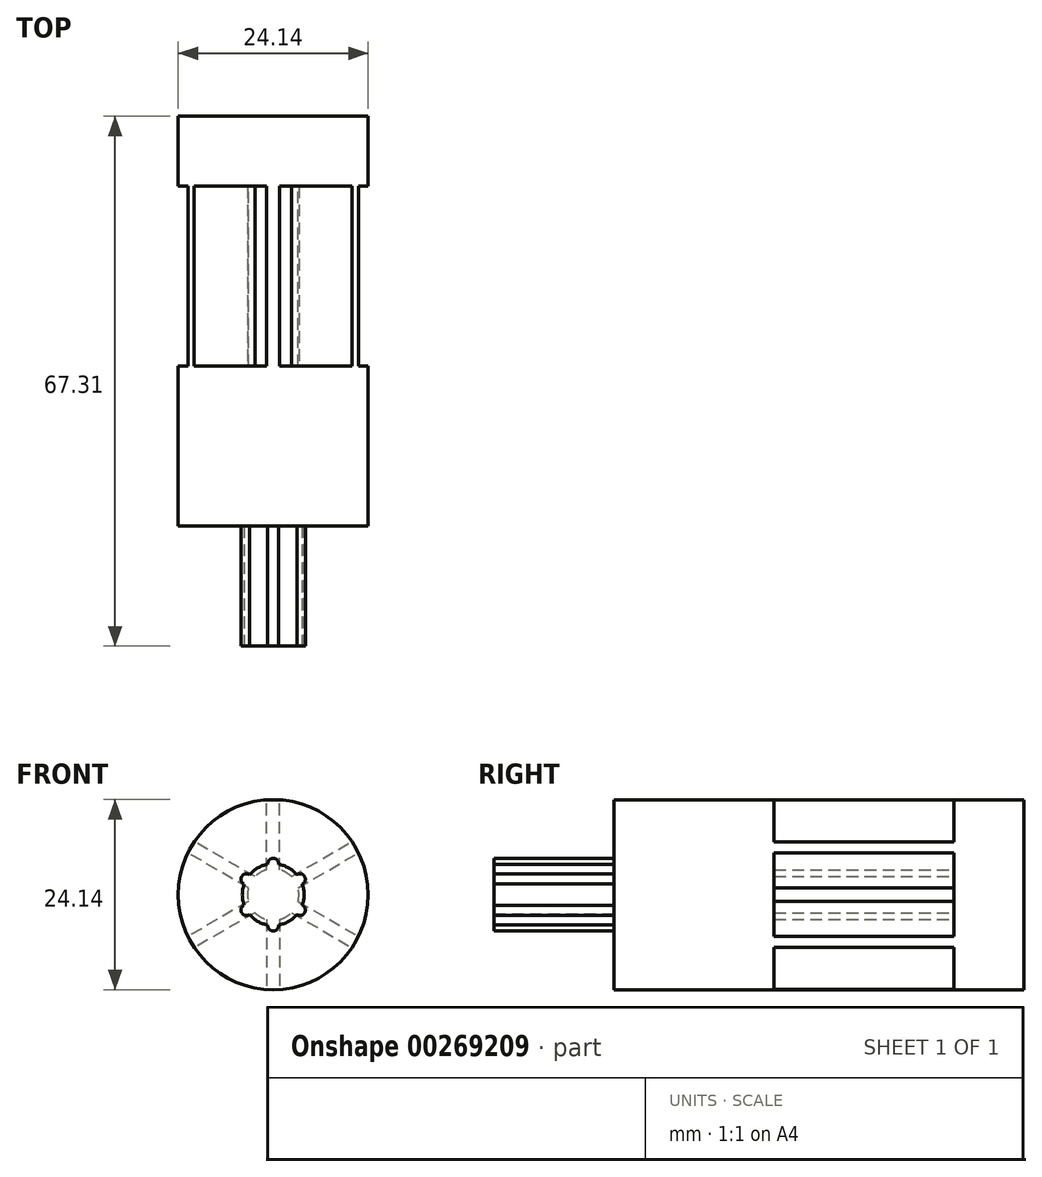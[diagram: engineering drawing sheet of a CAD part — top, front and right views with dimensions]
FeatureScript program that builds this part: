
annotation { "Feature Type Name" : "Feature", "Feature Type Description" : "" }
export const myFeature = defineFeature(function(context is Context, id is Id, definition is map)
    precondition{}
    {
        {
            var Q0;
            Q0=qCreatedBy(makeId("Front.planeOp"),FACE);
            var sketch = newSketch(context, id + "F0", { "sketchPlane" : qUnion([Q0])});
            skCircle(sketch, "E0", {"center": v(0, 0) * mm, "radius": 12.07 * mm});
            skCircle(sketch, "E1", {"center": v(0, 0) * mm, "radius": 3.27 * mm});
            skLineSegment(sketch, "E2", {"start": v(-0.82, 12.04) * mm, "end": v(-0.82, 3.16) * mm});
            skLineSegment(sketch, "E3.MirrorCS", {"start": v(0.82, 12.04) * mm, "end": v(0.82, 3.16) * mm});
            skLineSegment(sketch, "E4.1.0", {"start": v(-10.83, 5.31) * mm, "end": v(-3.15, 0.87) * mm});
            skLineSegment(sketch, "E4.1.1", {"start": v(-10.02, 6.73) * mm, "end": v(-2.33, 2.29) * mm});
            skLineSegment(sketch, "E4.2.0", {"start": v(-10.02, -6.73) * mm, "end": v(-2.33, -2.29) * mm});
            skLineSegment(sketch, "E4.2.1", {"start": v(-10.83, -5.31) * mm, "end": v(-3.15, -0.87) * mm});
            skLineSegment(sketch, "E4.3.0", {"start": v(0.82, -12.04) * mm, "end": v(0.82, -3.16) * mm});
            skLineSegment(sketch, "E4.3.1", {"start": v(-0.82, -12.04) * mm, "end": v(-0.82, -3.16) * mm});
            skLineSegment(sketch, "E4.4.0", {"start": v(10.83, -5.31) * mm, "end": v(3.15, -0.87) * mm});
            skLineSegment(sketch, "E4.4.1", {"start": v(10.02, -6.73) * mm, "end": v(2.33, -2.29) * mm});
            skLineSegment(sketch, "E4.5.0", {"start": v(10.02, 6.73) * mm, "end": v(2.33, 2.29) * mm});
            skLineSegment(sketch, "E4.5.1", {"start": v(10.83, 5.31) * mm, "end": v(3.15, 0.87) * mm});
            skSolve(sketch);
        }
        {
            var Q0;
            Q0=makeQuery(id+"F0.imprint","IMPRINT",FACE,{"disambiguationData":[TD([[makeQuery(id+"F0.imprint","IMPRINT",EDGE,{"derivedFrom":sQuery(id+"F0.wireOp",EDGE,"E1")}),1.0]])]});
            var Q1;
            Q1=makeQuery(id+"F0.imprint","IMPRINT",FACE,{"disambiguationData":[TD([[makeQuery(id+"F0.imprint","IMPRINT",EDGE,{"derivedFrom":sQuery(id+"F0.wireOp",EDGE,"E0")}),1.0]])]});
            extrude(context, id + "F1", {"entities" : qUnion([Q0, Q1]), "endBound" : BoundingType.SYMMETRIC, "depth" : 27.94 * mm});
        }
        {
            var Q0;
            Q0=makeQuery(id+"F0.imprint","IMPRINT",FACE,{"disambiguationData":[TD([[makeQuery(id+"F0.imprint","IMPRINT",EDGE,{"derivedFrom":sQuery(id+"F0.wireOp",EDGE,"E0")}),1.0]])]});
            extrude(context, id + "F2", {"entities" : qUnion([Q0]), "operationType" : NewBodyOperationType.REMOVE, "endBound" : BoundingType.SYMMETRIC, "oppositeDirection" : true, "depth" : 22.86 * mm});
        }
        {
            var Q0;
            {var subQ0=sQuery(id+"F0.wireOp",EDGE,"E2");Q0=makeQuery(id+"F0.imprint","IMPRINT",FACE,{"disambiguationData":[TD([[makeQuery(id+"F0.imprint","IMPRINT",EDGE,{"derivedFrom":subQ0}),1.0]])]});}
            var Q1;
            {var subQ0=sQuery(id+"F0.wireOp",EDGE,"E4.1.0");Q1=makeQuery(id+"F0.imprint","IMPRINT",FACE,{"disambiguationData":[TD([[makeQuery(id+"F0.imprint","IMPRINT",EDGE,{"derivedFrom":subQ0}),1.0]])]});}
            var Q2;
            {var subQ0=sQuery(id+"F0.wireOp",EDGE,"E4.2.0");Q2=makeQuery(id+"F0.imprint","IMPRINT",FACE,{"disambiguationData":[TD([[makeQuery(id+"F0.imprint","IMPRINT",EDGE,{"derivedFrom":subQ0}),1.0]])]});}
            var Q3;
            {var subQ0=sQuery(id+"F0.wireOp",EDGE,"E4.3.0");Q3=makeQuery(id+"F0.imprint","IMPRINT",FACE,{"disambiguationData":[TD([[makeQuery(id+"F0.imprint","IMPRINT",EDGE,{"derivedFrom":subQ0}),1.0]])]});}
            var Q4;
            {var subQ0=sQuery(id+"F0.wireOp",EDGE,"E4.5.0");Q4=makeQuery(id+"F0.imprint","IMPRINT",FACE,{"disambiguationData":[TD([[makeQuery(id+"F0.imprint","IMPRINT",EDGE,{"derivedFrom":subQ0}),1.0]])]});}
            var Q5;
            {var subQ0=sQuery(id+"F0.wireOp",EDGE,"E4.4.0");Q5=makeQuery(id+"F0.imprint","IMPRINT",FACE,{"disambiguationData":[TD([[makeQuery(id+"F0.imprint","IMPRINT",EDGE,{"derivedFrom":subQ0}),1.0]])]});}
            extrude(context, id + "F3", {"entities" : qUnion([Q0, Q1, Q2, Q3, Q4, Q5]), "operationType" : NewBodyOperationType.ADD, "endBound" : BoundingType.SYMMETRIC, "depth" : 25.4 * mm});
        }
        {
            var Q0;
            Q0=makeQuery(id+"F1.opExtrude","CAP_FACE",FACE,{"disambiguationData":[OSD([sQuery(id+"F0.wireOp",EDGE,"E0")])],"isStart":false});
            var sketch = newSketch(context, id + "F4", { "sketchPlane" : qUnion([Q0])});
            skCircle(sketch, "E5", {"center": v(0, 0) * mm, "radius": 3.92 * mm});
            skSolve(sketch);
        }
        {
            var Q0;
            Q0=makeQuery(id+"F4.imprint","IMPRINT",FACE,{"disambiguationData":[TD([[makeQuery(id+"F4.imprint","IMPRINT",EDGE,{"derivedFrom":sQuery(id+"F4.wireOp",EDGE,"E5")}),1.0]])]});
            extrude(context, id + "F5", {"entities" : qUnion([Q0]), "operationType" : NewBodyOperationType.ADD, "depth" : 12.7 * mm});
        }
        {
            var Q0;
            Q0=makeQuery(id+"F5.opExtrude","CAP_FACE",FACE,{"disambiguationData":[OSD([sQuery(id+"F4.wireOp",EDGE,"E5")])],"isStart":false});
            var sketch = newSketch(context, id + "F6", { "sketchPlane" : qUnion([Q0])});
            skCircle(sketch, "E6", {"center": v(0, 3.92) * mm, "radius": 0.69 * mm});
            skCircle(sketch, "E7.1.0", {"center": v(-3.4, 1.96) * mm, "radius": 0.69 * mm});
            skCircle(sketch, "E7.2.0", {"center": v(-3.4, -1.96) * mm, "radius": 0.69 * mm});
            skCircle(sketch, "E7.3.0", {"center": v(0, -3.92) * mm, "radius": 0.69 * mm});
            skCircle(sketch, "E7.4.0", {"center": v(3.4, -1.96) * mm, "radius": 0.69 * mm});
            skCircle(sketch, "E7.5.0", {"center": v(3.4, 1.96) * mm, "radius": 0.69 * mm});
            skPoint(sketch, "E7.center", {"position": v(0, 0) * mm});
            skSolve(sketch);
        }
        {
            var Q0;
            {var subQ0=sQuery(id+"F6.wireOp",EDGE,"E6");var subQ1=makeQuery(id+"F5.opExtrude","CAP_EDGE",EDGE,{"disambiguationData":[OSD([sQuery(id+"F4.wireOp",EDGE,"E5")])],"isStart":false});var subQ2=makeQuery(id+"F6.imprint","INTERSECT",VERTEX,{"disambiguationData":[OD(0.0)],"derivedFrom":[subQ1,subQ0]});Q0=makeQuery(id+"F6.imprint","IMPRINT",FACE,{"disambiguationData":[TD([[makeQuery(id+"F6.imprint","IMPRINT",EDGE,{"disambiguationData":[TD([[subQ2,1.0]])],"derivedFrom":subQ0}),1.0]])]});}
            var Q1;
            {var subQ0=sQuery(id+"F6.wireOp",EDGE,"E7.1.0");var subQ1=makeQuery(id+"F5.opExtrude","CAP_EDGE",EDGE,{"disambiguationData":[OSD([sQuery(id+"F4.wireOp",EDGE,"E5")])],"isStart":false});var subQ2=makeQuery(id+"F6.imprint","INTERSECT",VERTEX,{"disambiguationData":[OD(0.0)],"derivedFrom":[subQ1,subQ0]});Q1=makeQuery(id+"F6.imprint","IMPRINT",FACE,{"disambiguationData":[TD([[makeQuery(id+"F6.imprint","IMPRINT",EDGE,{"disambiguationData":[TD([[subQ2,1.0]])],"derivedFrom":subQ0}),1.0]])]});}
            var Q2;
            {var subQ0=sQuery(id+"F6.wireOp",EDGE,"E7.5.0");var subQ1=makeQuery(id+"F5.opExtrude","CAP_EDGE",EDGE,{"disambiguationData":[OSD([sQuery(id+"F4.wireOp",EDGE,"E5")])],"isStart":false});var subQ2=makeQuery(id+"F6.imprint","INTERSECT",VERTEX,{"disambiguationData":[OD(0.0)],"derivedFrom":[subQ1,subQ0]});Q2=makeQuery(id+"F6.imprint","IMPRINT",FACE,{"disambiguationData":[TD([[makeQuery(id+"F6.imprint","IMPRINT",EDGE,{"disambiguationData":[TD([[subQ2,1.0]])],"derivedFrom":subQ0}),1.0]])]});}
            var Q3;
            {var subQ0=sQuery(id+"F6.wireOp",EDGE,"E7.4.0");var subQ1=makeQuery(id+"F5.opExtrude","CAP_EDGE",EDGE,{"disambiguationData":[OSD([sQuery(id+"F4.wireOp",EDGE,"E5")])],"isStart":false});var subQ2=makeQuery(id+"F6.imprint","INTERSECT",VERTEX,{"disambiguationData":[OD(0.0)],"derivedFrom":[subQ1,subQ0]});Q3=makeQuery(id+"F6.imprint","IMPRINT",FACE,{"disambiguationData":[TD([[makeQuery(id+"F6.imprint","IMPRINT",EDGE,{"disambiguationData":[TD([[subQ2,-1.0]])],"derivedFrom":subQ0}),1.0]])]});}
            var Q4;
            {var subQ0=sQuery(id+"F6.wireOp",EDGE,"E7.3.0");var subQ1=makeQuery(id+"F5.opExtrude","CAP_EDGE",EDGE,{"disambiguationData":[OSD([sQuery(id+"F4.wireOp",EDGE,"E5")])],"isStart":false});var subQ2=makeQuery(id+"F6.imprint","INTERSECT",VERTEX,{"disambiguationData":[OD(0.0)],"derivedFrom":[subQ1,subQ0]});Q4=makeQuery(id+"F6.imprint","IMPRINT",FACE,{"disambiguationData":[TD([[makeQuery(id+"F6.imprint","IMPRINT",EDGE,{"disambiguationData":[TD([[subQ2,-1.0]])],"derivedFrom":subQ0}),1.0]])]});}
            var Q5;
            {var subQ0=sQuery(id+"F6.wireOp",EDGE,"E7.2.0");var subQ1=makeQuery(id+"F5.opExtrude","CAP_EDGE",EDGE,{"disambiguationData":[OSD([sQuery(id+"F4.wireOp",EDGE,"E5")])],"isStart":false});var subQ2=makeQuery(id+"F6.imprint","INTERSECT",VERTEX,{"disambiguationData":[OD(0.0)],"derivedFrom":[subQ1,subQ0]});Q5=makeQuery(id+"F6.imprint","IMPRINT",FACE,{"disambiguationData":[TD([[makeQuery(id+"F6.imprint","IMPRINT",EDGE,{"disambiguationData":[TD([[subQ2,-1.0]])],"derivedFrom":subQ0}),1.0]])]});}
            extrude(context, id + "F7", {"entities" : qUnion([Q0, Q1, Q2, Q3, Q4, Q5]), "operationType" : NewBodyOperationType.ADD, "oppositeDirection" : true, "depth" : 14.1 * mm});
        }
        {
            var Q0;
            {var subQ0=sQuery(id+"F4.wireOp",EDGE,"E5");Q0=makeQuery(id+"F7.boolean.opBoolean","MERGE",FACE,{"derivedFrom":[makeQuery(id+"F5.opExtrude","CAP_FACE",FACE,{"disambiguationData":[OSD([subQ0])],"isStart":false}),makeQuery(id+"F7.opExtrude","CAP_FACE",FACE,{"disambiguationData":[OSD([subQ0,sQuery(id+"F6.wireOp",EDGE,"E6")])],"isStart":true}),makeQuery(id+"F7.opExtrude","CAP_FACE",FACE,{"disambiguationData":[OSD([subQ0,sQuery(id+"F6.wireOp",EDGE,"E7.1.0")])],"isStart":true}),makeQuery(id+"F7.opExtrude","CAP_FACE",FACE,{"disambiguationData":[OSD([subQ0,sQuery(id+"F6.wireOp",EDGE,"E7.2.0")])],"isStart":true}),makeQuery(id+"F7.opExtrude","CAP_FACE",FACE,{"disambiguationData":[OSD([subQ0,sQuery(id+"F6.wireOp",EDGE,"E7.3.0")])],"isStart":true}),makeQuery(id+"F7.opExtrude","CAP_FACE",FACE,{"disambiguationData":[OSD([subQ0,sQuery(id+"F6.wireOp",EDGE,"E7.4.0")])],"isStart":true}),makeQuery(id+"F7.opExtrude","CAP_FACE",FACE,{"disambiguationData":[OSD([subQ0,sQuery(id+"F6.wireOp",EDGE,"E7.5.0")])],"isStart":true})]});}
            extrude(context, id + "F8", {"entities" : qUnion([Q0]), "operationType" : NewBodyOperationType.ADD, "depth" : 12.7 * mm});
        }
        {
            var Q0;
            Q0=makeQuery(id+"F1.opExtrude","CAP_FACE",FACE,{"disambiguationData":[OSD([sQuery(id+"F0.wireOp",EDGE,"E0")])],"isStart":false});
            extrude(context, id + "F9", {"entities" : qUnion([Q0]), "operationType" : NewBodyOperationType.ADD, "depth" : 5.08 * mm});
        }
        {
            var Q0;
            Q0=makeQuery(id+"F1.opExtrude","CAP_FACE",FACE,{"disambiguationData":[OSD([sQuery(id+"F0.wireOp",EDGE,"E0")])],"isStart":true});
            extrude(context, id + "F10", {"entities" : qUnion([Q0]), "operationType" : NewBodyOperationType.ADD, "depth" : 6.35 * mm});
        }
        {
            var Q0;
            Q0=makeQuery(id+"F9.opExtrude","CAP_FACE",FACE,{"disambiguationData":[OSD([sQuery(id+"F0.wireOp",EDGE,"E0")])],"isStart":false});
            extrude(context, id + "F11", {"entities" : qUnion([Q0]), "operationType" : NewBodyOperationType.ADD, "depth" : 12.7 * mm});
        }
        {
            var Q0;
            Q0=makeQuery(id+"F8.opExtrude","CAP_FACE",FACE,{"disambiguationData":[OSD([sQuery(id+"F4.wireOp",EDGE,"E5"),sQuery(id+"F6.wireOp",EDGE,"E6"),sQuery(id+"F6.wireOp",EDGE,"E7.1.0"),sQuery(id+"F6.wireOp",EDGE,"E7.2.0"),sQuery(id+"F6.wireOp",EDGE,"E7.3.0"),sQuery(id+"F6.wireOp",EDGE,"E7.4.0"),sQuery(id+"F6.wireOp",EDGE,"E7.5.0")])],"isStart":false});
            extrude(context, id + "F12", {"entities" : qUnion([Q0]), "operationType" : NewBodyOperationType.ADD, "depth" : 7.62 * mm});
        }
    });
